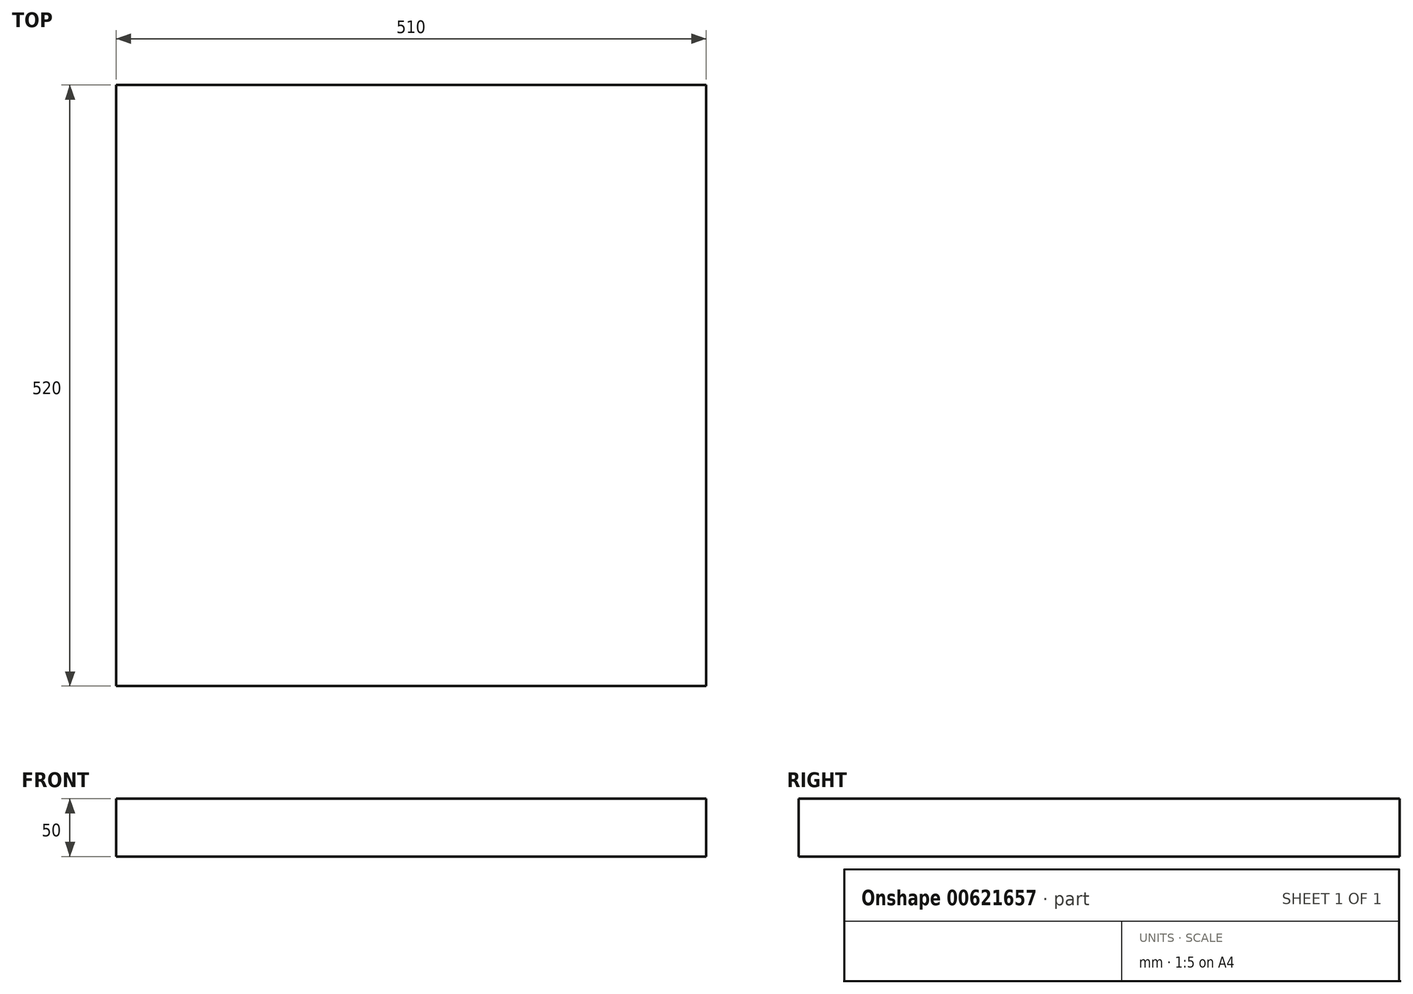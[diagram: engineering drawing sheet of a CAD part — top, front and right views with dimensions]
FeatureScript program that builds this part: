
annotation { "Feature Type Name" : "Feature", "Feature Type Description" : "" }
export const myFeature = defineFeature(function(context is Context, id is Id, definition is map)
    precondition{}
    {
        {
            var Q0;
            Q0=qCreatedBy(makeId("Top.planeOp"),FACE);
            var sketch = newSketch(context, id + "F0", { "sketchPlane" : qUnion([Q0])});
            skLineSegment(sketch, "E0.bottom", {"start": v(0, 0) * mm, "end": v(510, 0) * mm});
            skLineSegment(sketch, "E0.top", {"start": v(0, 520) * mm, "end": v(510, 520) * mm});
            skLineSegment(sketch, "E0.left", {"start": v(0, 0) * mm, "end": v(0, 520) * mm});
            skLineSegment(sketch, "E0.right", {"start": v(510, 0) * mm, "end": v(510, 520) * mm});
            skSolve(sketch);
        }
        {
            var Q0;
            Q0 = qSketchRegion(id + "F0", true);
            extrude(context, id + "F1", {"entities" : qUnion([Q0]), "depth" : 50 * mm, "offsetDistance" : 25 * mm});
        }
    });
